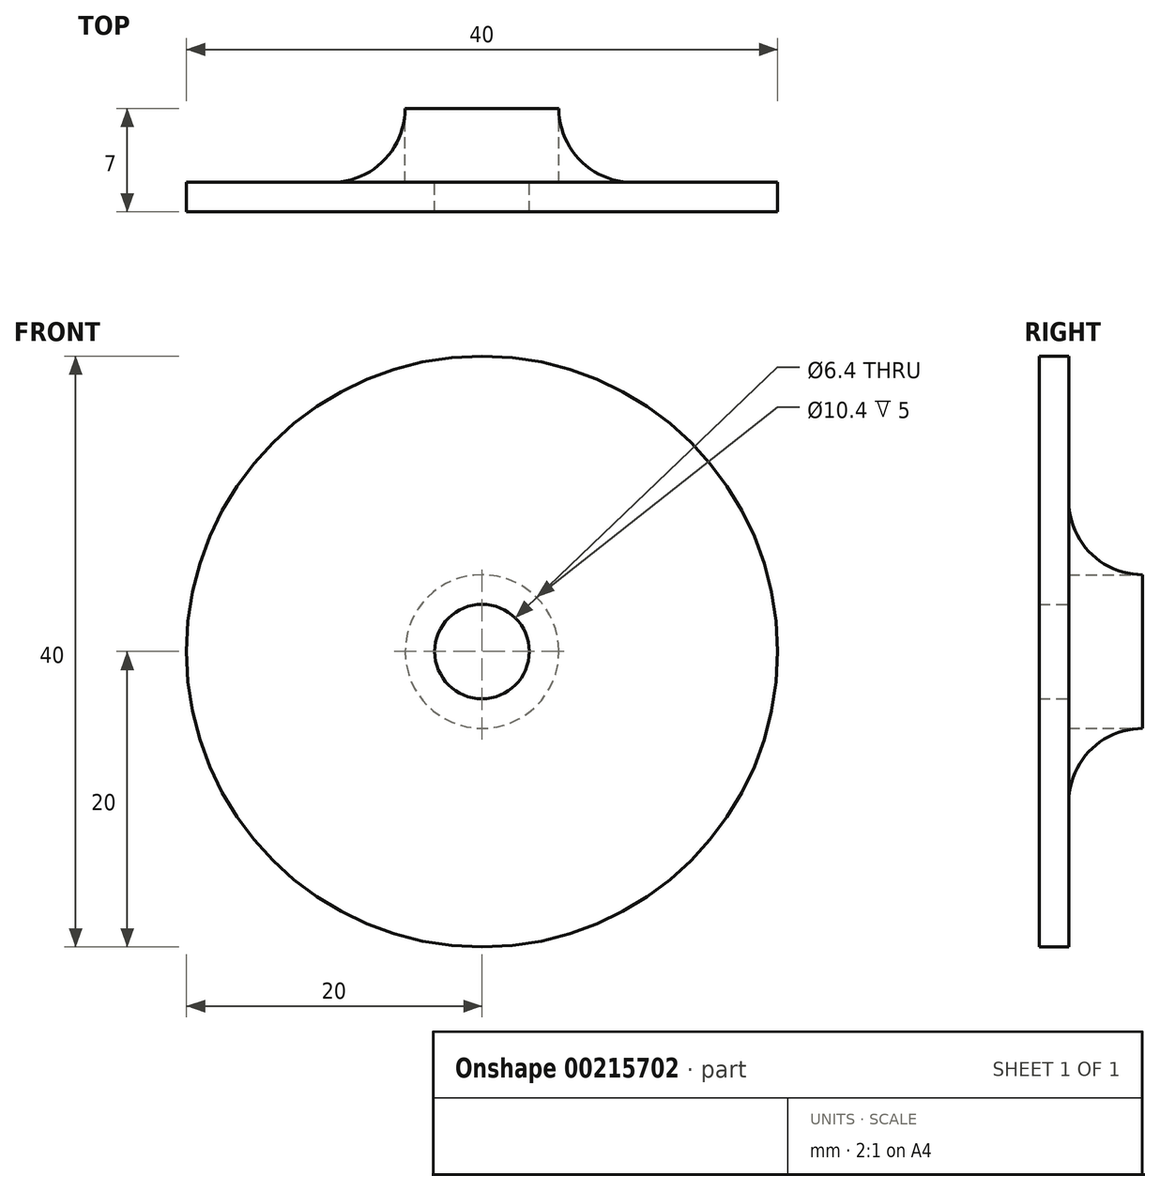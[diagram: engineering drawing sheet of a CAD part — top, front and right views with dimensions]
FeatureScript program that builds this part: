
annotation { "Feature Type Name" : "Feature", "Feature Type Description" : "" }
export const myFeature = defineFeature(function(context is Context, id is Id, definition is map)
    precondition{}
    {
        {
            var Q0;
            Q0=qCreatedBy(makeId("Top.planeOp"),FACE);
            var sketch = newSketch(context, id + "F0", { "sketchPlane" : qUnion([Q0])});
            skLineSegment(sketch, "E0", {"start": v(-3.2, 2) * mm, "end": v(-5.2, 2) * mm});
            skLineSegment(sketch, "E1", {"start": v(-5.2, 2) * mm, "end": v(-5.2, 7) * mm});
            skLineSegment(sketch, "E2", {"start": v(-10.2, 2) * mm, "end": v(-20, 2) * mm});
            skLineSegment(sketch, "E3", {"start": v(-20, 2) * mm, "end": v(-20, 0) * mm});
            skLineSegment(sketch, "E4", {"start": v(-20, 0) * mm, "end": v(-3.2, 0) * mm});
            skLineSegment(sketch, "E5", {"start": v(-3.2, 0) * mm, "end": v(-3.2, 2) * mm});
            skLineSegment(sketch, "E6", {"start": v(0, 11.54) * mm, "end": v(0, -15.77) * mm, "construction": true});
            skArc(sketch, "E7", {"start": v(-10.2, 2) * mm, "mid": v(-6.66, 3.46) * mm, "end": v(-5.2, 7) * mm});
            skSolve(sketch);
        }
        {
            var Q0;
            Q0 = qSketchRegion(id + "F0", true);
            var Q1;
            Q1=sQuery(id+"F0.wireOp",EDGE,"E6");
            revolve(context, id + "F1", {"entities" : qUnion([Q0]), "axis" : qUnion([Q1]), "revolveType" : RevolveType.FULL});
        }
    });
